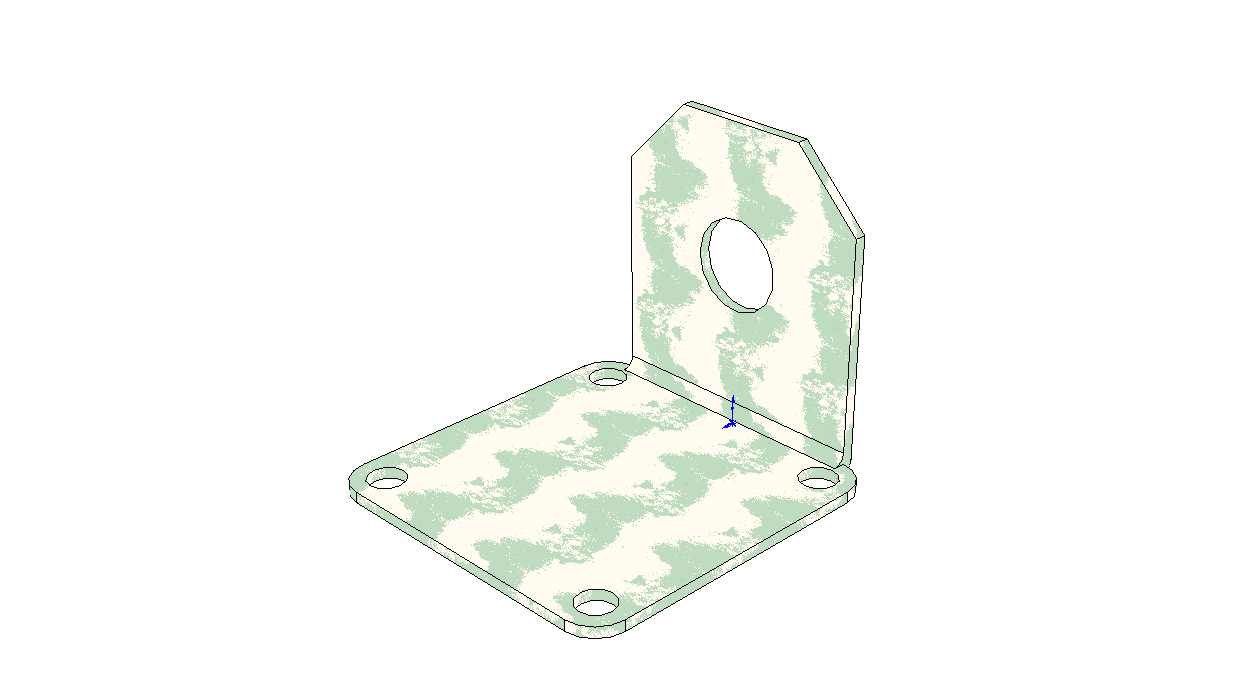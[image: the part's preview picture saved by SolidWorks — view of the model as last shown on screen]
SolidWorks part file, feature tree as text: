
SOLIDWORKS PART (.sldprt)
format: sldprt  version: not decoded by parser v0  size: 202,752 bytes
history: native  units: mm
features: plane x3, sketch x3, cut_extrude x2, material x1, extrude x1, fillet x1 (+8 scaffold rows collapsed)
feature tree (19):
  scaffold x8  (default folders/planes/origin — collapsed)
  material  "Matériau <non spécifié>"
  plane  "Plan de face"
  plane  "Plan de dessus"
  plane  "Plan de droite"
  sketch  "Esquisse1"  dims[c1.D10=1.6mm c1.D14=3.0mm c1.D1=30.0mm c1.D2=15.0mm c1.D3=30.0mm c1.D4=15.0mm c1.D5=12.0mm c1.D6=24.0mm c1.D7=1.0mm c1.D8=3.0mm c1.D9=3.0mm c2.D10=26.3mm c2.D11=6.0mm c2.D12=6.0mm c2.D13=12.0mm]
  extrude  "Extrusion1"  Depth=26.4mm
  sketch  "Esquisse13"  dims[D4=~2.286641mm D1=6.0mm D2=6.0mm D3=12.0mm]
  sketch  "Esquisse14"
  cut_extrude  "Enlèv. mat.-Extru.1"  Depth=25.4mm
  cut_extrude  "Enlèv. mat.-Extru.2"  Depth=2mm
  fillet  "Congé1"  Radius=1mm
decode coverage: 6 of 7 modeling features carry decoded parameters
note: ~ marks probable driven/reference dimensions
note: suppression state not decoded; provenance and decode notes live in map.json
